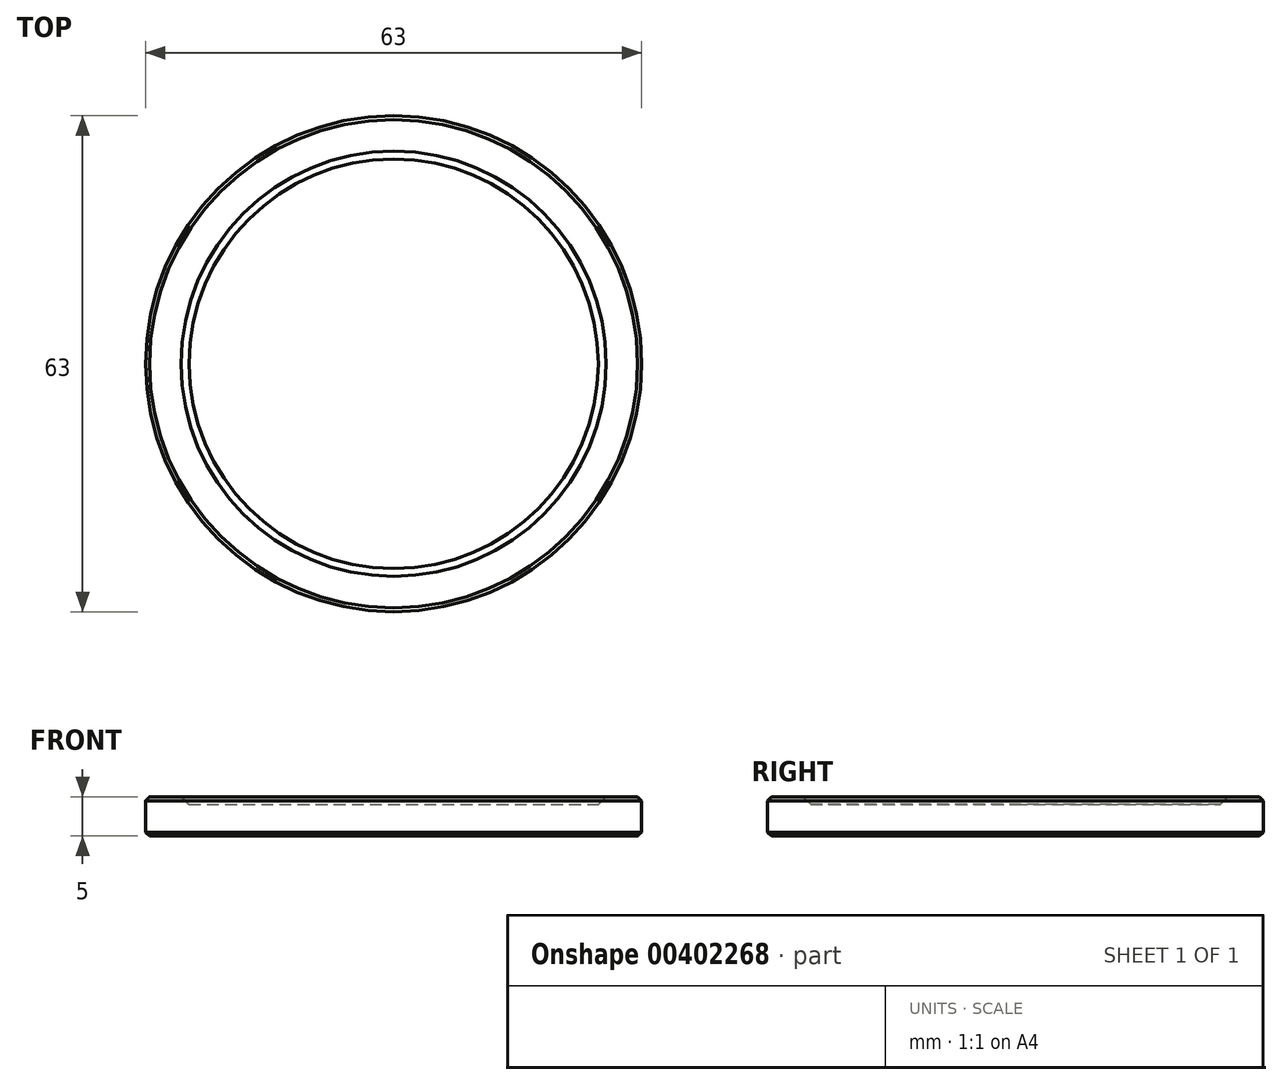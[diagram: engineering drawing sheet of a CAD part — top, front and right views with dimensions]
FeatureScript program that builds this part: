
annotation { "Feature Type Name" : "Feature", "Feature Type Description" : "" }
export const myFeature = defineFeature(function(context is Context, id is Id, definition is map)
    precondition{}
    {
        {
            var Q0;
            Q0=qCreatedBy(makeId("Front.planeOp"),FACE);
            var sketch = newSketch(context, id + "F0", { "sketchPlane" : qUnion([Q0])});
            skLineSegment(sketch, "E0", {"start": v(0, 0) * mm, "end": v(-31.5, 0) * mm});
            skLineSegment(sketch, "E1", {"start": v(-31.5, 0) * mm, "end": v(-31.5, 5) * mm});
            skLineSegment(sketch, "E2", {"start": v(-31.5, 5) * mm, "end": v(-26.5, 5) * mm});
            skLineSegment(sketch, "E3", {"start": v(-26.5, 5) * mm, "end": v(-26.5, 4) * mm});
            skLineSegment(sketch, "E4", {"start": v(-26.5, 4) * mm, "end": v(0, 4) * mm});
            skLineSegment(sketch, "E5", {"start": v(0, 4) * mm, "end": v(0, 0) * mm});
            skSolve(sketch);
        }
        {
            var Q0;
            Q0=makeQuery(id+"F0.imprint","IMPRINT",FACE,{"disambiguationData":[TD([[makeQuery(id+"F0.imprint","IMPRINT",EDGE,{"derivedFrom":sQuery(id+"F0.wireOp",EDGE,"E0")}),-1.0]])]});
            var Q1;
            Q1=sQuery(id+"F0.wireOp",EDGE,"E5");
            revolve(context, id + "F1", {"entities" : qUnion([Q0]), "axis" : qUnion([Q1]), "revolveType" : RevolveType.FULL});
        }
        {
            var Q0;
            Q0=makeQuery(id+"F1.opRevolve","SWEPT_EDGE",EDGE,{"disambiguationData":[OSD([sQuery(id+"F0.wireOp",EDGE,"E3"),sQuery(id+"F0.wireOp",EDGE,"E4")])]});
            var Q1;
            Q1=makeQuery(id+"F1.opRevolve","SWEPT_EDGE",EDGE,{"disambiguationData":[OSD([sQuery(id+"F0.wireOp",EDGE,"E2"),sQuery(id+"F0.wireOp",EDGE,"E3")])]});
            var Q2;
            Q2=makeQuery(id+"F1.opRevolve","SWEPT_EDGE",EDGE,{"disambiguationData":[OSD([sQuery(id+"F0.wireOp",EDGE,"E1"),sQuery(id+"F0.wireOp",EDGE,"E2")])]});
            var Q3;
            Q3=makeQuery(id+"F1.opRevolve","SWEPT_EDGE",EDGE,{"disambiguationData":[OSD([sQuery(id+"F0.wireOp",EDGE,"E0"),sQuery(id+"F0.wireOp",EDGE,"E1")])]});
            chamfer(context, id + "F2", {"entities" : qUnion([Q0, Q1, Q2, Q3]), "width" : .5 * mm, "tangentPropagation" : true});
        }
    });
